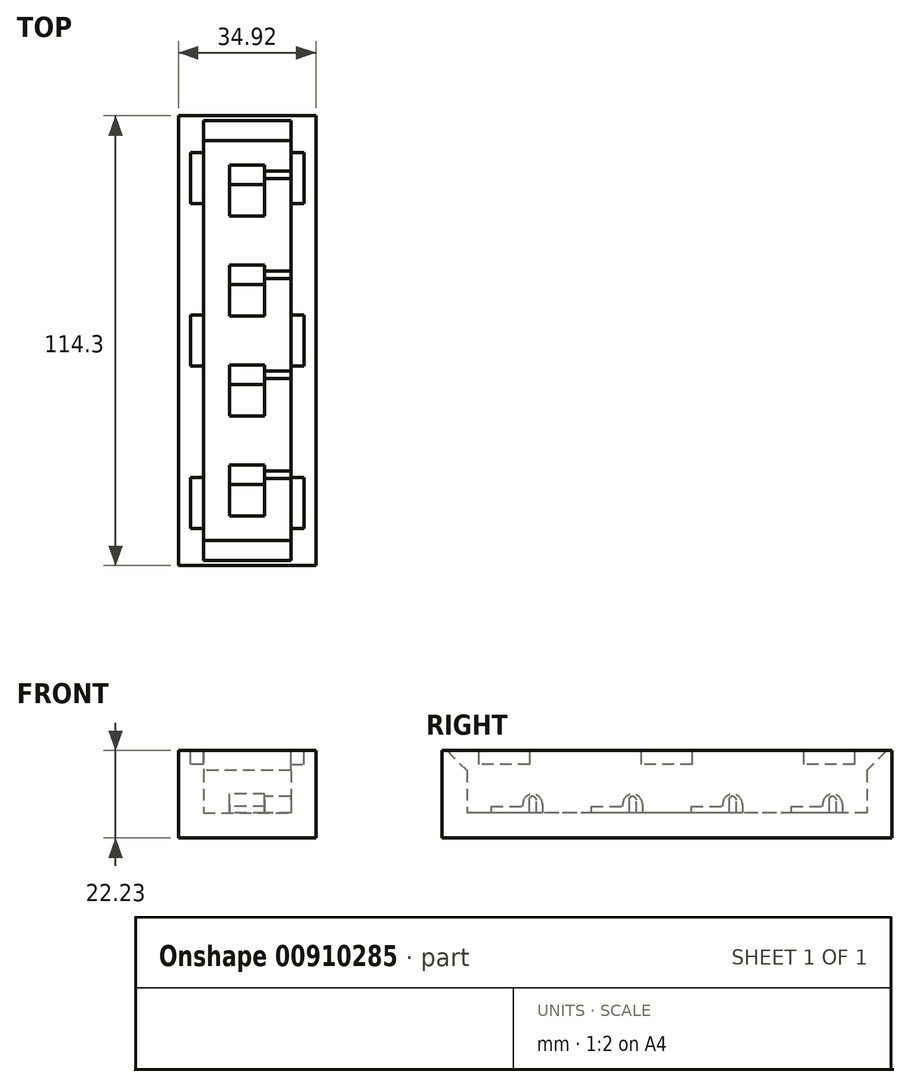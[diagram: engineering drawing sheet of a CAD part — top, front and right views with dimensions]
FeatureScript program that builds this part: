
annotation { "Feature Type Name" : "Feature", "Feature Type Description" : "" }
export const myFeature = defineFeature(function(context is Context, id is Id, definition is map)
    precondition{}
    {
        {
            var Q0;
            Q0=qCreatedBy(makeId("Top.planeOp"),FACE);
            var sketch = newSketch(context, id + "F0", { "sketchPlane" : qUnion([Q0])});
            skLineSegment(sketch, "E0.bottom", {"start": v(-11.11, 50.8) * mm, "end": v(11.11, 50.8) * mm});
            skLineSegment(sketch, "E0.top", {"start": v(-11.11, -50.8) * mm, "end": v(11.11, -50.8) * mm});
            skLineSegment(sketch, "E0.left", {"start": v(-11.11, 50.8) * mm, "end": v(-11.11, -50.8) * mm});
            skLineSegment(sketch, "E0.right", {"start": v(11.11, 50.8) * mm, "end": v(11.11, -50.8) * mm});
            skLineSegment(sketch, "E1", {"start": v(-11.11, 50.8) * mm, "end": v(11.11, -50.8) * mm, "construction": true});
            skLineSegment(sketch, "E2", {"start": v(11.11, 50.8) * mm, "end": v(-11.11, -50.8) * mm, "construction": true});
            skPoint(sketch, "E3", {"position": v(0, 0) * mm});
            skSolve(sketch);
        }
        {
            var Q0;
            Q0 = qSketchRegion(id + "F0", true);
            extrude(context, id + "F1", {"entities" : qUnion([Q0]), "oppositeDirection" : true, "depth" : 6.35 * mm, "offsetDistance" : 25.4 * mm});
        }
        {
            var Q0;
            Q0=qCreatedBy(makeId("Right.planeOp"),FACE);
            var sketch = newSketch(context, id + "F2", { "sketchPlane" : qUnion([Q0])});
            skLineSegment(sketch, "E4", {"start": v(-31.62, 0) * mm, "end": v(-44.58, 0) * mm});
            skLineSegment(sketch, "E5", {"start": v(-44.58, 0) * mm, "end": v(-44.58, 1.65) * mm});
            skLineSegment(sketch, "E6", {"start": v(-44.58, 1.65) * mm, "end": v(-36.58, 1.65) * mm});
            skLineSegment(sketch, "E7", {"start": v(-36.58, 1.65) * mm, "end": v(-36.58, 2.35) * mm});
            skLineSegment(sketch, "E8", {"start": v(-31.62, 2.35) * mm, "end": v(-31.62, 0) * mm});
            skArc(sketch, "E9.trimOffspring", {"start": v(-31.62, 2.35) * mm, "mid": v(-34.1, 4.83) * mm, "end": v(-36.58, 2.35) * mm});
            skLineSegment(sketch, "E10", {"start": v(-38.1, 0) * mm, "end": v(-38.1, 5.07) * mm, "construction": true});
            skLineSegment(sketch, "E11.1.0.0", {"start": v(-6.22, 0) * mm, "end": v(-19.18, 0) * mm});
            skLineSegment(sketch, "E11.1.0.1", {"start": v(-19.18, 0) * mm, "end": v(-19.18, 1.65) * mm});
            skLineSegment(sketch, "E11.1.0.2", {"start": v(-19.18, 1.65) * mm, "end": v(-11.18, 1.65) * mm});
            skLineSegment(sketch, "E11.1.0.3", {"start": v(-11.18, 1.65) * mm, "end": v(-11.18, 2.35) * mm});
            skArc(sketch, "E11.1.0.4", {"start": v(-6.22, 2.35) * mm, "mid": v(-8.7, 4.83) * mm, "end": v(-11.18, 2.35) * mm});
            skLineSegment(sketch, "E11.1.0.5", {"start": v(-6.22, 2.35) * mm, "end": v(-6.22, 0) * mm});
            skLineSegment(sketch, "E11.1.0.6", {"start": v(-12.7, 0) * mm, "end": v(-12.7, 5.07) * mm, "construction": true});
            skLineSegment(sketch, "E11.2.0.0", {"start": v(19.18, 0) * mm, "end": v(6.22, 0) * mm});
            skLineSegment(sketch, "E11.2.0.1", {"start": v(6.22, 0) * mm, "end": v(6.22, 1.65) * mm});
            skLineSegment(sketch, "E11.2.0.2", {"start": v(6.22, 1.65) * mm, "end": v(14.22, 1.65) * mm});
            skLineSegment(sketch, "E11.2.0.3", {"start": v(14.22, 1.65) * mm, "end": v(14.22, 2.35) * mm});
            skArc(sketch, "E11.2.0.4", {"start": v(19.18, 2.35) * mm, "mid": v(16.7, 4.83) * mm, "end": v(14.22, 2.35) * mm});
            skLineSegment(sketch, "E11.2.0.5", {"start": v(19.18, 2.35) * mm, "end": v(19.18, 0) * mm});
            skLineSegment(sketch, "E11.2.0.6", {"start": v(12.7, 0) * mm, "end": v(12.7, 5.07) * mm, "construction": true});
            skLineSegment(sketch, "E11.3.0.0", {"start": v(44.58, 0) * mm, "end": v(31.62, 0) * mm});
            skLineSegment(sketch, "E11.3.0.1", {"start": v(31.62, 0) * mm, "end": v(31.62, 1.65) * mm});
            skLineSegment(sketch, "E11.3.0.2", {"start": v(31.62, 1.65) * mm, "end": v(39.62, 1.65) * mm});
            skLineSegment(sketch, "E11.3.0.3", {"start": v(39.62, 1.65) * mm, "end": v(39.62, 2.35) * mm});
            skArc(sketch, "E11.3.0.4", {"start": v(44.58, 2.35) * mm, "mid": v(42.1, 4.83) * mm, "end": v(39.62, 2.35) * mm});
            skLineSegment(sketch, "E11.3.0.5", {"start": v(44.58, 2.35) * mm, "end": v(44.58, 0) * mm});
            skLineSegment(sketch, "E11.3.0.6", {"start": v(38.1, 0) * mm, "end": v(38.1, 5.07) * mm, "construction": true});
            skLineSegment(sketch, "E11.direction1", {"start": v(-44.58, 0) * mm, "end": v(-19.18, 0) * mm, "construction": true});
            skSolve(sketch);
        }
        {
            var Q0;
            Q0 = qSketchRegion(id + "F2", true);
            extrude(context, id + "F3", {"entities" : qUnion([Q0]), "operationType" : NewBodyOperationType.ADD, "endBound" : BoundingType.SYMMETRIC, "depth" : 8.9 * mm, "offsetDistance" : 25.4 * mm});
        }
        {
            var Q0;
            Q0=makeQuery(id+"F3.opExtrude","CAP_FACE",FACE,{"disambiguationData":[OSD([sQuery(id+"F2.wireOp",EDGE,"E4"),sQuery(id+"F2.wireOp",EDGE,"E5"),sQuery(id+"F2.wireOp",EDGE,"E6"),sQuery(id+"F2.wireOp",EDGE,"E7"),sQuery(id+"F2.wireOp",EDGE,"E8"),sQuery(id+"F2.wireOp",EDGE,"E9.trimOffspring")])],"isStart":false});
            var sketch = newSketch(context, id + "F4", { "sketchPlane" : qUnion([Q0])});
            skLineSegment(sketch, "E12", {"start": v(-37.68, 4.25) * mm, "end": v(-30.52, 4.25) * mm, "construction": true});
            skLineSegment(sketch, "E13", {"start": v(-34.1, 0) * mm, "end": v(-34.1, 4.25) * mm, "construction": true});
            skPoint(sketch, "E13.endSnap0", {"position": v(-34.1, 4.25) * mm});
            skPoint(sketch, "E14", {"position": v(-34.1, 2.35) * mm});
            skCircle(sketch, "E15", {"center": v(-34.1, 3.3) * mm, "radius": 0.95 * mm, "construction": true});
            skLineSegment(sketch, "E16", {"start": v(-35.05, 3.3) * mm, "end": v(-35.05, 0) * mm});
            skLineSegment(sketch, "E17", {"start": v(-35.05, 0) * mm, "end": v(-33.15, 0) * mm});
            skLineSegment(sketch, "E18", {"start": v(-33.15, 0) * mm, "end": v(-33.15, 3.3) * mm});
            skArc(sketch, "E19", {"start": v(-33.15, 3.3) * mm, "mid": v(-34.1, 4.25) * mm, "end": v(-35.05, 3.3) * mm});
            skLineSegment(sketch, "E20.1.0.0", {"start": v(-9.65, 0) * mm, "end": v(-7.75, 0) * mm});
            skLineSegment(sketch, "E20.1.0.1", {"start": v(-9.65, 3.3) * mm, "end": v(-9.65, 0) * mm});
            skArc(sketch, "E20.1.0.2", {"start": v(-7.75, 3.3) * mm, "mid": v(-8.7, 4.25) * mm, "end": v(-9.65, 3.3) * mm});
            skLineSegment(sketch, "E20.1.0.3", {"start": v(-7.75, 0) * mm, "end": v(-7.75, 3.3) * mm});
            skLineSegment(sketch, "E20.2.0.0", {"start": v(15.75, 0) * mm, "end": v(17.65, 0) * mm});
            skLineSegment(sketch, "E20.2.0.1", {"start": v(15.75, 3.3) * mm, "end": v(15.75, 0) * mm});
            skArc(sketch, "E20.2.0.2", {"start": v(17.65, 3.3) * mm, "mid": v(16.7, 4.25) * mm, "end": v(15.75, 3.3) * mm});
            skLineSegment(sketch, "E20.2.0.3", {"start": v(17.65, 0) * mm, "end": v(17.65, 3.3) * mm});
            skLineSegment(sketch, "E20.3.0.0", {"start": v(41.15, 0) * mm, "end": v(43.05, 0) * mm});
            skLineSegment(sketch, "E20.3.0.1", {"start": v(41.15, 3.3) * mm, "end": v(41.15, 0) * mm});
            skArc(sketch, "E20.3.0.2", {"start": v(43.05, 3.3) * mm, "mid": v(42.1, 4.25) * mm, "end": v(41.15, 3.3) * mm});
            skLineSegment(sketch, "E20.3.0.3", {"start": v(43.05, 0) * mm, "end": v(43.05, 3.3) * mm});
            skLineSegment(sketch, "E20.direction1", {"start": v(-35.05, 0) * mm, "end": v(-9.65, 0) * mm, "construction": true});
            skSolve(sketch);
        }
        {
            var Q0;
            Q0 = qSketchRegion(id + "F4", true);
            var Q1;
            Q1=makeQuery(id+"F1.opExtrude","SWEPT_FACE",FACE,{"disambiguationData":[OSD([sQuery(id+"F0.wireOp",EDGE,"E0.right")])]});
            extrude(context, id + "F5", {"entities" : qUnion([Q0]), "operationType" : NewBodyOperationType.ADD, "endBound" : BoundingType.UP_TO_SURFACE, "depth" : 25.4 * mm, "endBoundEntityFace" : qUnion([Q1]), "offsetDistance" : 25.4 * mm});
        }
        {
            var Q0;
            Q0=makeQuery(id+"F1.opExtrude","CAP_FACE",FACE,{"disambiguationData":[OSD([sQuery(id+"F0.wireOp",EDGE,"E0.bottom"),sQuery(id+"F0.wireOp",EDGE,"E0.top"),sQuery(id+"F0.wireOp",EDGE,"E0.left"),sQuery(id+"F0.wireOp",EDGE,"E0.right")])],"isStart":false});
            var sketch = newSketch(context, id + "F6", { "sketchPlane" : qUnion([Q0])});
            skLineSegment(sketch, "E21.0", {"start": v(-11.11, 50.8) * mm, "end": v(11.11, 50.8) * mm});
            skLineSegment(sketch, "E22.0", {"start": v(11.11, -50.8) * mm, "end": v(11.11, 50.8) * mm});
            skLineSegment(sketch, "E23.0", {"start": v(-11.11, -50.8) * mm, "end": v(11.11, -50.8) * mm});
            skLineSegment(sketch, "E24.0", {"start": v(-11.11, -50.8) * mm, "end": v(-11.11, 50.8) * mm});
            skLineSegment(sketch, "E25.0", {"start": v(-17.46, 57.15) * mm, "end": v(17.46, 57.15) * mm});
            skLineSegment(sketch, "E25.1", {"start": v(-17.46, -57.15) * mm, "end": v(-17.46, 57.15) * mm});
            skLineSegment(sketch, "E25.2", {"start": v(-17.46, -57.15) * mm, "end": v(17.46, -57.15) * mm});
            skLineSegment(sketch, "E25.3", {"start": v(17.46, -57.15) * mm, "end": v(17.46, 57.15) * mm});
            skSolve(sketch);
        }
        {
            var Q0;
            Q0 = qSketchRegion(id + "F6", true);
            extrude(context, id + "F7", {"entities" : qUnion([Q0]), "operationType" : NewBodyOperationType.ADD, "oppositeDirection" : true, "depth" : 22.22 * mm, "offsetDistance" : 25.4 * mm});
        }
        {
            var Q0;
            Q0=makeQuery(id+"F7.opExtrude","CAP_FACE",FACE,{"disambiguationData":[OSD([sQuery(id+"F6.wireOp",EDGE,"E21.0"),sQuery(id+"F6.wireOp",EDGE,"E22.0"),sQuery(id+"F6.wireOp",EDGE,"E23.0"),sQuery(id+"F6.wireOp",EDGE,"E24.0"),sQuery(id+"F6.wireOp",EDGE,"E25.0"),sQuery(id+"F6.wireOp",EDGE,"E25.1"),sQuery(id+"F6.wireOp",EDGE,"E25.2"),sQuery(id+"F6.wireOp",EDGE,"E25.3")])],"isStart":false});
            var sketch = newSketch(context, id + "F8", { "sketchPlane" : qUnion([Q0])});
            skLineSegment(sketch, "E26.bottom", {"start": v(-11.11, 47.75) * mm, "end": v(-14.41, 47.75) * mm});
            skLineSegment(sketch, "E26.top", {"start": v(-11.11, 34.8) * mm, "end": v(-14.41, 34.8) * mm});
            skLineSegment(sketch, "E26.left", {"start": v(-11.11, 47.75) * mm, "end": v(-11.11, 34.8) * mm});
            skLineSegment(sketch, "E26.right", {"start": v(-14.41, 47.75) * mm, "end": v(-14.41, 34.8) * mm});
            skLineSegment(sketch, "E27.bottom", {"start": v(-11.11, 6.48) * mm, "end": v(-14.41, 6.48) * mm});
            skLineSegment(sketch, "E27.top", {"start": v(-11.11, -6.48) * mm, "end": v(-14.41, -6.48) * mm});
            skLineSegment(sketch, "E27.left", {"start": v(-11.11, 6.48) * mm, "end": v(-11.11, -6.48) * mm});
            skLineSegment(sketch, "E27.right", {"start": v(-14.41, 6.48) * mm, "end": v(-14.41, -6.48) * mm});
            skLineSegment(sketch, "E28.bottom", {"start": v(-11.11, -47.75) * mm, "end": v(-14.41, -47.75) * mm});
            skLineSegment(sketch, "E28.top", {"start": v(-11.11, -34.8) * mm, "end": v(-14.41, -34.8) * mm});
            skLineSegment(sketch, "E28.left", {"start": v(-11.11, -47.75) * mm, "end": v(-11.11, -34.8) * mm});
            skLineSegment(sketch, "E28.right", {"start": v(-14.41, -47.75) * mm, "end": v(-14.41, -34.8) * mm});
            skLineSegment(sketch, "E29", {"start": v(-14.41, 0) * mm, "end": v(-11.11, 0) * mm, "construction": true});
            skLineSegment(sketch, "E30.MirrorCS", {"start": v(11.11, 47.75) * mm, "end": v(14.41, 47.75) * mm});
            skLineSegment(sketch, "E31.MirrorCS", {"start": v(11.11, 47.75) * mm, "end": v(11.11, 34.8) * mm});
            skLineSegment(sketch, "E32.MirrorCS", {"start": v(14.41, 47.75) * mm, "end": v(14.41, 34.8) * mm});
            skLineSegment(sketch, "E33.MirrorCS", {"start": v(11.11, 34.8) * mm, "end": v(14.41, 34.8) * mm});
            skLineSegment(sketch, "E34.MirrorCS", {"start": v(11.11, -6.48) * mm, "end": v(14.41, -6.48) * mm});
            skLineSegment(sketch, "E35.MirrorCS", {"start": v(14.41, 6.48) * mm, "end": v(14.41, -6.48) * mm});
            skLineSegment(sketch, "E36.MirrorCS", {"start": v(11.11, 6.48) * mm, "end": v(14.41, 6.48) * mm});
            skLineSegment(sketch, "E37.MirrorCS", {"start": v(11.11, 6.48) * mm, "end": v(11.11, -6.48) * mm});
            skLineSegment(sketch, "E38.MirrorCS", {"start": v(11.11, -47.75) * mm, "end": v(14.41, -47.75) * mm});
            skLineSegment(sketch, "E39.MirrorCS", {"start": v(14.41, -47.75) * mm, "end": v(14.41, -34.8) * mm});
            skLineSegment(sketch, "E40.MirrorCS", {"start": v(11.11, -34.8) * mm, "end": v(14.41, -34.8) * mm});
            skLineSegment(sketch, "E41.MirrorCS", {"start": v(11.11, -47.75) * mm, "end": v(11.11, -34.8) * mm});
            skSolve(sketch);
        }
        {
            var Q0;
            Q0 = qSketchRegion(id + "F8", true);
            extrude(context, id + "F9", {"entities" : qUnion([Q0]), "operationType" : NewBodyOperationType.REMOVE, "oppositeDirection" : true, "depth" : 3.5 * mm, "offsetDistance" : 25.4 * mm});
        }
        {
            var Q0;
            Q0=makeQuery(id+"F7.opExtrude","CAP_EDGE",EDGE,{"disambiguationData":[OSD([sQuery(id+"F6.wireOp",EDGE,"E23.0")])],"isStart":false});
            var Q1;
            Q1=makeQuery(id+"F7.opExtrude","CAP_EDGE",EDGE,{"disambiguationData":[OSD([sQuery(id+"F6.wireOp",EDGE,"E21.0")])],"isStart":false});
            chamfer(context, id + "F10", {"entities" : qUnion([Q0, Q1]), "width" : 5.08 * mm, "tangentPropagation" : true});
        }
    });
